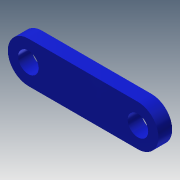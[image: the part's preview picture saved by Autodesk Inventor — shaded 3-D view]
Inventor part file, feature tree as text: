
AUTODESK INVENTOR PART (.ipt)
format: ipt  version: 2013 (Build 170138000, 138)  size: 94,720 bytes
history: native  units: mm
features: extrude x2, sketch x2
ambient origin geometry x8: Origin, YZ Plane, XZ Plane, XY Plane, X Axis, Y Axis, Z Axis, Center Point
bodies: Solid1 (feature_tree)
feature tree (4):
  extrude  "Extrusion1"  Depth=6.0mm
  extrude  "Extrusion2"  Depth=6.0mm
  sketch  "Sketch1"  dims[d0=16.0mm d1=6.0mm]
  sketch  "Sketch2"  dims[d2=6.0mm d3=6.0mm d4=2.0mm d5=0.0mm d6=3.0mm d7=3.0mm d8=2.0mm d9=0.0mm]
